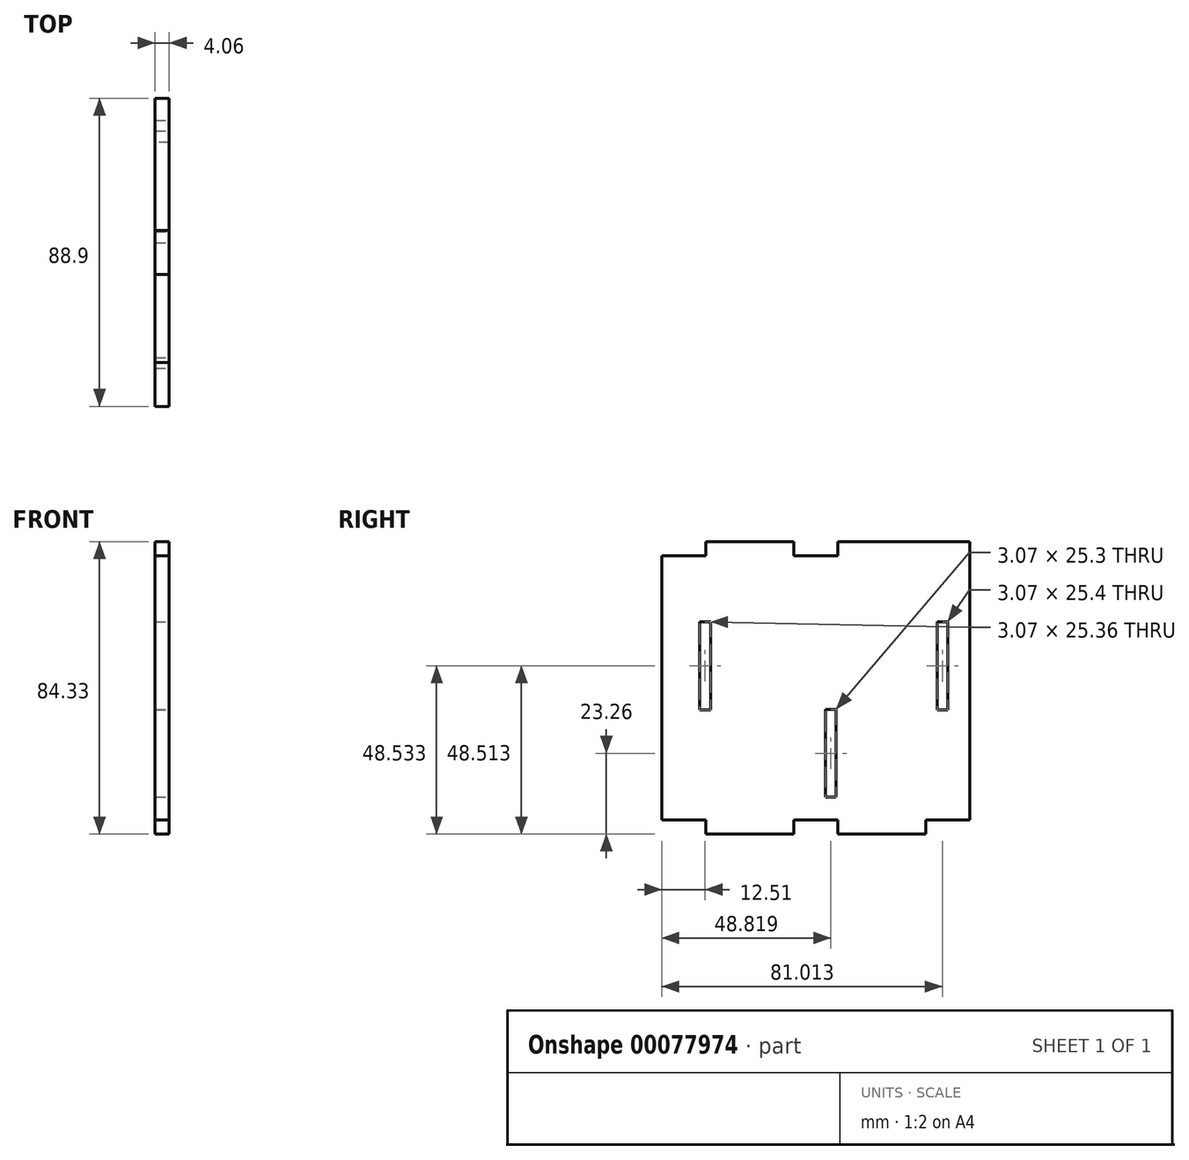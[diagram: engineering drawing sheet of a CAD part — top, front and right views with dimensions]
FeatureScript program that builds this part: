
annotation { "Feature Type Name" : "Feature", "Feature Type Description" : "" }
export const myFeature = defineFeature(function(context is Context, id is Id, definition is map)
    precondition{}
    {
        {
            var Q0;
            Q0=qCreatedBy(makeId("Right.planeOp"),FACE);
            var sketch = newSketch(context, id + "F0", { "sketchPlane" : qUnion([Q0])});
            skLineSegment(sketch, "E0.left", {"start": v(50.8, 39.26) * mm, "end": v(50.8, -36.94) * mm});
            skLineSegment(sketch, "E0.right", {"start": v(-38.1, 39.26) * mm, "end": v(-38.1, -36.94) * mm});
            skLineSegment(sketch, "E1", {"start": v(50.8, 1.16) * mm, "end": v(-38.1, 1.16) * mm});
            skLineSegment(sketch, "E2", {"start": v(12.7, 39.26) * mm, "end": v(0, 39.26) * mm});
            skLineSegment(sketch, "E3", {"start": v(38.1, 43.33) * mm, "end": v(12.7, 43.33) * mm});
            skLineSegment(sketch, "E4", {"start": v(-25.4, 43.33) * mm, "end": v(-25.4, 39.26) * mm});
            skLineSegment(sketch, "E5.left", {"start": v(12.7, 39.26) * mm, "end": v(12.7, 43.33) * mm});
            skLineSegment(sketch, "E5.right", {"start": v(0, 39.26) * mm, "end": v(0, 43.33) * mm});
            skLineSegment(sketch, "E6.trimOffspring", {"start": v(0, 43.33) * mm, "end": v(-25.4, 43.33) * mm});
            skLineSegment(sketch, "E7.trimOffspring", {"start": v(-25.4, 39.26) * mm, "end": v(-38.1, 39.26) * mm});
            skLineSegment(sketch, "E8.MirrorCS", {"start": v(38.1, -41) * mm, "end": v(12.7, -41) * mm});
            skLineSegment(sketch, "E9.MirrorCS", {"start": v(12.7, -36.94) * mm, "end": v(12.7, -41) * mm});
            skLineSegment(sketch, "E10.MirrorCS", {"start": v(0, -36.94) * mm, "end": v(0, -41) * mm});
            skLineSegment(sketch, "E11.MirrorCS", {"start": v(0, -41) * mm, "end": v(-25.4, -41) * mm});
            skLineSegment(sketch, "E12.MirrorCS", {"start": v(-25.4, -41) * mm, "end": v(-25.4, -36.94) * mm});
            skLineSegment(sketch, "E13.trimOffspring", {"start": v(12.7, -36.94) * mm, "end": v(0, -36.94) * mm});
            skLineSegment(sketch, "E14.trimOffspring", {"start": v(-25.4, -36.94) * mm, "end": v(-38.1, -36.94) * mm});
            skLineSegment(sketch, "E15.bottom", {"start": v(38.1, 43.33) * mm, "end": v(50.8, 43.33) * mm});
            skLineSegment(sketch, "E15.right", {"start": v(50.8, 43.33) * mm, "end": v(50.8, 39.26) * mm});
            skPoint(sketch, "E16.MirrorCS.start.orphan", {"position": v(38.1, -36.94) * mm});
            skPoint(sketch, "E0.bottom.end.orphan", {"position": v(38.1, 39.26) * mm});
            skLineSegment(sketch, "E17", {"start": v(38.1, -36.94) * mm, "end": v(50.8, -36.94) * mm});
            skLineSegment(sketch, "E18", {"start": v(38.1, -41) * mm, "end": v(38.1, -36.94) * mm});
            skSolve(sketch);
        }
        {
            var Q0;
            Q0=qSketchRegion(id+"F0",true);
            extrude(context, id + "F1", {"entities" : qUnion([Q0]), "depth" : 4.06 * mm});
        }
        {
            var Q0;
            Q0=makeQuery(id+"F1.opExtrude","CAP_FACE",FACE,{"disambiguationData":[OSD([sQuery(id+"F0.wireOp",EDGE,"E0.top"),sQuery(id+"F0.wireOp",EDGE,"E0.left"),sQuery(id+"F0.wireOp",EDGE,"E0.right"),sQuery(id+"F0.wireOp",EDGE,"n29zO06o-gDxo-vX3y-oJDm-HRG5ElsrULuQ"),sQuery(id+"F0.wireOp",EDGE,"4MnWMn7D-OnMf-LYy8-2Vb4-XY7oqSbkhUoS"),sQuery(id+"F0.wireOp",EDGE,"E3"),sQuery(id+"F0.wireOp",EDGE,"E4"),sQuery(id+"F0.wireOp",EDGE,"E5.left"),sQuery(id+"F0.wireOp",EDGE,"E5.right"),sQuery(id+"F0.wireOp",EDGE,"E6.trimOffspring"),sQuery(id+"F0.wireOp",EDGE,"E2"),sQuery(id+"F0.wireOp",EDGE,"E7.trimOffspring"),sQuery(id+"F0.wireOp",EDGE,"E16.MirrorCS"),sQuery(id+"F0.wireOp",EDGE,"E8.MirrorCS"),sQuery(id+"F0.wireOp",EDGE,"E9.MirrorCS"),sQuery(id+"F0.wireOp",EDGE,"E10.MirrorCS"),sQuery(id+"F0.wireOp",EDGE,"E11.MirrorCS"),sQuery(id+"F0.wireOp",EDGE,"E12.MirrorCS"),sQuery(id+"F0.wireOp",EDGE,"E13.trimOffspring"),sQuery(id+"F0.wireOp",EDGE,"E14.trimOffspring")])],"isStart":false});
            var sketch = newSketch(context, id + "F2", { "sketchPlane" : qUnion([Q0])});
            skLineSegment(sketch, "E19", {"start": v(50.8, -36.94) * mm, "end": v(50.8, -36.94) * mm});
            skLineSegment(sketch, "E20.MirrorCS", {"start": v(-27.13, 20.21) * mm, "end": v(-27.13, -5.15) * mm});
            skLineSegment(sketch, "E21.MirrorCS", {"start": v(-27.13, 20.21) * mm, "end": v(-24.05, 20.21) * mm});
            skLineSegment(sketch, "E22.MirrorCS", {"start": v(-27.13, -5.15) * mm, "end": v(-24.05, -5.15) * mm});
            skLineSegment(sketch, "E23", {"start": v(-24.05, 20.21) * mm, "end": v(-24.05, -5.15) * mm});
            skLineSegment(sketch, "E24.0", {"start": v(9.18, 7.61) * mm, "end": v(9.18, 32.91) * mm});
            skLineSegment(sketch, "E25", {"start": v(9.18, 32.91) * mm, "end": v(12.26, 32.91) * mm});
            skLineSegment(sketch, "E26.bottom", {"start": v(12.26, 32.91) * mm, "end": v(9.18, 32.91) * mm});
            skLineSegment(sketch, "E26.top", {"start": v(12.26, 7.61) * mm, "end": v(9.18, 7.61) * mm});
            skLineSegment(sketch, "E26.left", {"start": v(12.26, 32.91) * mm, "end": v(12.26, 7.61) * mm});
            skLineSegment(sketch, "E26.right", {"start": v(9.18, 32.91) * mm, "end": v(9.18, 7.61) * mm});
            skLineSegment(sketch, "E27.MirrorCS", {"start": v(12.26, -5.09) * mm, "end": v(9.18, -5.09) * mm});
            skLineSegment(sketch, "E28.MirrorCS", {"start": v(12.26, -30.4) * mm, "end": v(12.26, -5.09) * mm});
            skLineSegment(sketch, "E29.MirrorCS", {"start": v(9.18, -5.09) * mm, "end": v(9.18, -30.4) * mm});
            skLineSegment(sketch, "E30.MirrorCS", {"start": v(9.18, -30.4) * mm, "end": v(12.26, -30.4) * mm});
            skLineSegment(sketch, "E31", {"start": v(50.8, 20.21) * mm, "end": v(44.45, 20.21) * mm});
            skLineSegment(sketch, "E32", {"start": v(44.45, 20.21) * mm, "end": v(44.45, -5.19) * mm});
            skLineSegment(sketch, "E33.0", {"start": v(41.38, 20.21) * mm, "end": v(41.38, -5.19) * mm});
            skLineSegment(sketch, "E34", {"start": v(41.38, 20.21) * mm, "end": v(44.45, 20.21) * mm});
            skLineSegment(sketch, "E35", {"start": v(44.45, -5.19) * mm, "end": v(41.38, -5.19) * mm});
            skSolve(sketch);
        }
        {
            var Q0;
            Q0=makeQuery(id+"F2.imprint","IMPRINT",FACE,{"disambiguationData":[TD([[makeQuery(id+"F2.imprint","IMPRINT",EDGE,{"derivedFrom":sQuery(id+"F2.wireOp",EDGE,"E20.MirrorCS")}),1.0]])]});
            var Q1;
            Q1=makeQuery(id+"F2.imprint","IMPRINT",FACE,{"disambiguationData":[TD([[makeQuery(id+"F2.imprint","IMPRINT",EDGE,{"derivedFrom":sQuery(id+"F2.wireOp",EDGE,"E26.bottom")}),1.0]])]});
            var Q2;
            Q2=makeQuery(id+"F2.imprint","IMPRINT",FACE,{"disambiguationData":[TD([[makeQuery(id+"F2.imprint","IMPRINT",EDGE,{"derivedFrom":sQuery(id+"F2.wireOp",EDGE,"E27.MirrorCS")}),1.0]])]});
            var Q3;
            Q3=makeQuery(id+"F2.imprint","IMPRINT",FACE,{"disambiguationData":[TD([[makeQuery(id+"F2.imprint","IMPRINT",EDGE,{"derivedFrom":sQuery(id+"F2.wireOp",EDGE,"E32")}),-1.0]])]});
            extrude(context, id + "F3", {"entities" : qUnion([Q0, Q1, Q2, Q3]), "operationType" : NewBodyOperationType.REMOVE, "oppositeDirection" : true, "depth" : 25.4 * mm});
        }
    });
